# Revit family: CENTUM Hammerschraube, gezahnt
name_source: partatom
category: HLS-Bauteile
revit_build: Autodesk Revit 2017 (Build: 20190507_1515(x64)
units: mm (PartAtom-declared; Revit-internal decimal feet)

## family parameters
Arbeitsebenenbasiert = Nein
Beim Laden mit Abzugskörper schneiden = Nein
Bemaßung runder Anschluss = Durchmesser verwenden
Gemeinsam genutzt = Ja
Immer vertikal = Nein
Raumberechnungspunkt = Nein
Teiletyp = Normal

## types (1)
- CENTUM Sperrscheibe FK10
    Artikelnummer = 1610019000/zn
    B = 23 mm
    D = 13 mm
    D0 = 13 mm
    EAN = 4250928448170
    Fabrikat = MEFA
    Festigkeitsklasse = 10
    Firma = MEFA Befestigungs- und Montagesysteme GmbH
    Gewicht = 0.03 kg
    Gewicht pro Bauteil = 0.03 kg
    Kurztext1 = Sperrscheibe CENTUM
    Kurztext2 = d1 12,3 mm 23.5 x 23.5 x 10 mm
    L = 24 mm
    L1 = 34 mm
    Länge Gewinde = 0 mm  [stored 0 ft]
    Material = Stahl
    Mengeneinheit = St
    Oberflaeche = Zink-Nickel
    S = 10 mm  [stored 0.0328084 ft]
    d1 = 11 mm
    vpe = 100 St

note: [stored X ft] marks values corroborated as IEEE doubles in the binary element streams (Revit-internal decimal feet)
